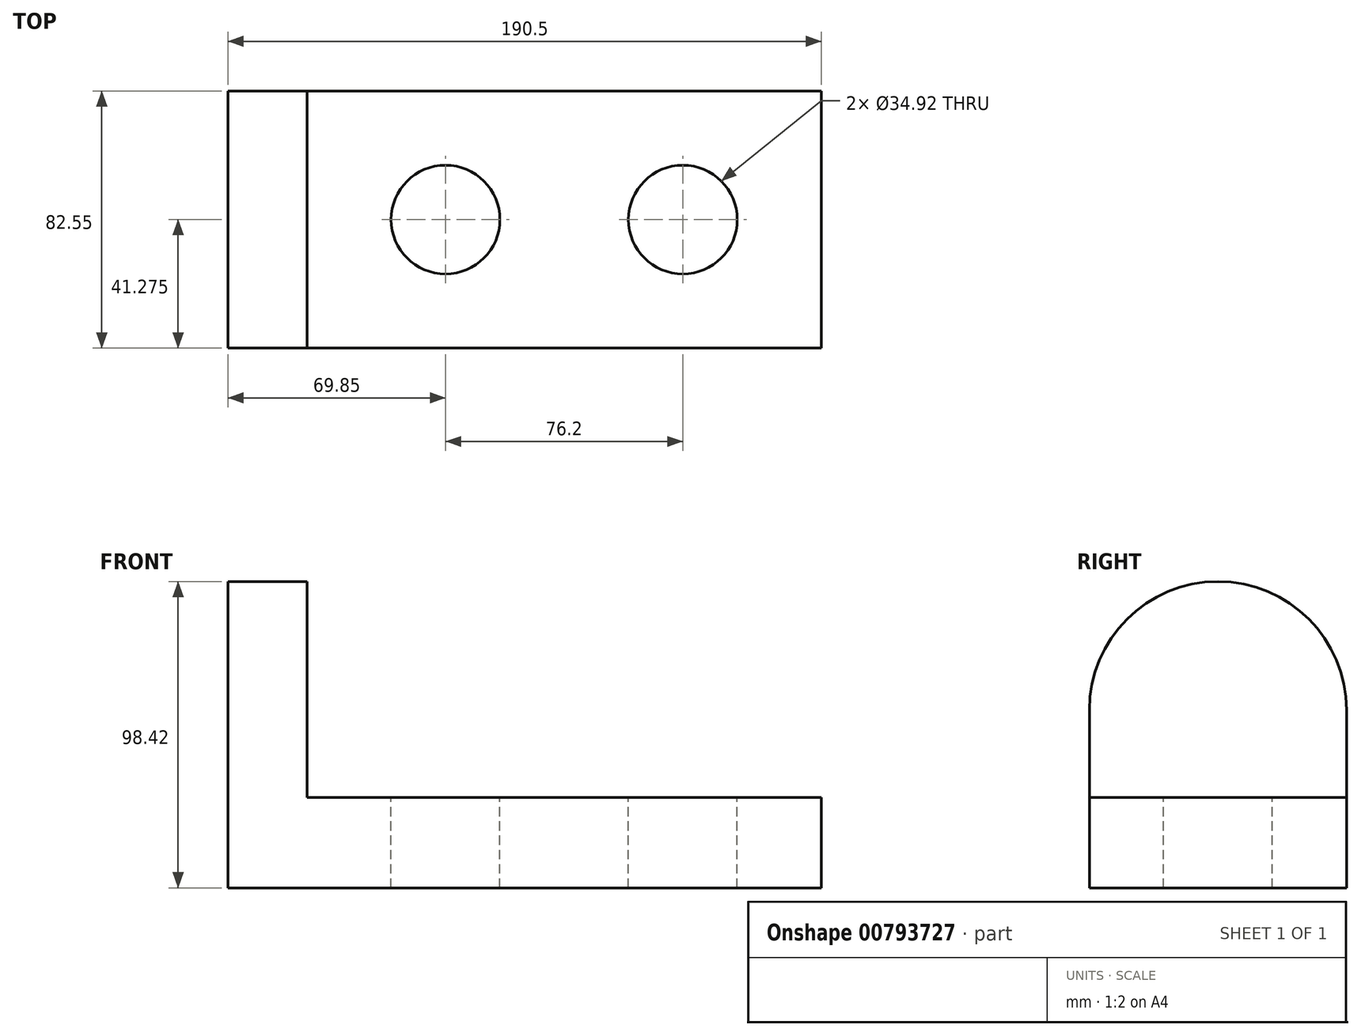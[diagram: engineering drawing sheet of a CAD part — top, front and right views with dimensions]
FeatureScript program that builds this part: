
annotation { "Feature Type Name" : "Feature", "Feature Type Description" : "" }
export const myFeature = defineFeature(function(context is Context, id is Id, definition is map)
    precondition{}
    {
        {
            var Q0;
            Q0=qCreatedBy(makeId("Front.planeOp"),FACE);
            var sketch = newSketch(context, id + "F0", { "sketchPlane" : qUnion([Q0])});
            skLineSegment(sketch, "E0", {"start": v(0, 0) * mm, "end": v(0, 101.6) * mm});
            skLineSegment(sketch, "E1", {"start": v(0, 101.6) * mm, "end": v(25.4, 101.6) * mm});
            skLineSegment(sketch, "E2", {"start": v(0, 0) * mm, "end": v(190.5, 0) * mm});
            skLineSegment(sketch, "E3", {"start": v(190.5, 0) * mm, "end": v(190.5, 29) * mm});
            skLineSegment(sketch, "E4", {"start": v(190.5, 29) * mm, "end": v(25.4, 29) * mm});
            skLineSegment(sketch, "E5", {"start": v(25.4, 29) * mm, "end": v(25.4, 101.6) * mm});
            skSolve(sketch);
        }
        {
            var Q0;
            Q0=makeQuery(id+"F0.imprint","IMPRINT",FACE,{"disambiguationData":[TD([[makeQuery(id+"F0.imprint","IMPRINT",EDGE,{"derivedFrom":sQuery(id+"F0.wireOp",EDGE,"E0")}),-1.0]])]});
            extrude(context, id + "F1", {"entities" : qUnion([Q0]), "depth" : 82.55 * mm, "offsetDistance" : 25.4 * mm});
        }
        {
            var Q0;
            Q0=makeQuery(id+"F1.opExtrude","SWEPT_FACE",FACE,{"disambiguationData":[OSD([sQuery(id+"F0.wireOp",EDGE,"E0")])]});
            var sketch = newSketch(context, id + "F2", { "sketchPlane" : qUnion([Q0])});
            skLineSegment(sketch, "E6", {"start": v(0, 0) * mm, "end": v(0, 57.15) * mm});
            skLineSegment(sketch, "E7", {"start": v(82.55, 0) * mm, "end": v(82.55, 57.15) * mm});
            skLineSegment(sketch, "E8", {"start": v(0, 57.15) * mm, "end": v(41.28, 57.15) * mm});
            skLineSegment(sketch, "E9", {"start": v(41.28, 57.15) * mm, "end": v(82.55, 57.15) * mm});
            skArc(sketch, "E10", {"start": v(82.55, 57.15) * mm, "mid": v(41.28, 98.43) * mm, "end": v(0, 57.15) * mm});
            skSolve(sketch);
        }
        {
            var Q0;
            {var subQ0=sQuery(id+"F2.wireOp",EDGE,"E10");Q0=makeQuery(id+"F2.imprint","IMPRINT",FACE,{"disambiguationData":[TD([[makeQuery(id+"F2.imprint","IMPRINT",EDGE,{"derivedFrom":subQ0}),-1.0]])]});}
            extrude(context, id + "F3", {"entities" : qUnion([Q0]), "operationType" : NewBodyOperationType.REMOVE, "endBound" : BoundingType.THROUGH_ALL, "oppositeDirection" : true, "depth" : 25.4 * mm, "offsetDistance" : 25.4 * mm});
        }
        {
            var Q0;
            Q0=makeQuery(id+"F1.opExtrude","SWEPT_FACE",FACE,{"disambiguationData":[OSD([sQuery(id+"F0.wireOp",EDGE,"E4")])]});
            var sketch = newSketch(context, id + "F4", { "sketchPlane" : qUnion([Q0])});
            skLineSegment(sketch, "E11", {"start": v(25.4, 0) * mm, "end": v(69.85, 0) * mm, "construction": true});
            skLineSegment(sketch, "E12", {"start": v(69.85, 0) * mm, "end": v(146.05, 0) * mm, "construction": true});
            skLineSegment(sketch, "E13", {"start": v(146.05, 0) * mm, "end": v(190.5, 0) * mm, "construction": true});
            skLineSegment(sketch, "E14", {"start": v(69.85, 0) * mm, "end": v(69.85, -41.28) * mm, "construction": true});
            skLineSegment(sketch, "E15", {"start": v(69.85, -41.28) * mm, "end": v(69.85, -82.55) * mm, "construction": true});
            skLineSegment(sketch, "E16", {"start": v(146.05, 0) * mm, "end": v(146.05, -41.28) * mm, "construction": true});
            skLineSegment(sketch, "E17", {"start": v(146.05, -41.28) * mm, "end": v(146.05, -82.55) * mm, "construction": true});
            skCircle(sketch, "E18", {"center": v(69.85, -41.28) * mm, "radius": 17.46 * mm});
            skCircle(sketch, "E19", {"center": v(146.05, -41.28) * mm, "radius": 17.46 * mm});
            skSolve(sketch);
        }
        {
            var Q0;
            Q0=makeQuery(id+"F4.imprint","IMPRINT",FACE,{"disambiguationData":[TD([[makeQuery(id+"F4.imprint","IMPRINT",EDGE,{"derivedFrom":sQuery(id+"F4.wireOp",EDGE,"E18")}),1.0]])]});
            var Q1;
            Q1=makeQuery(id+"F4.imprint","IMPRINT",FACE,{"disambiguationData":[TD([[makeQuery(id+"F4.imprint","IMPRINT",EDGE,{"derivedFrom":sQuery(id+"F4.wireOp",EDGE,"E19")}),1.0]])]});
            extrude(context, id + "F5", {"entities" : qUnion([Q0, Q1]), "operationType" : NewBodyOperationType.REMOVE, "endBound" : BoundingType.THROUGH_ALL, "oppositeDirection" : true, "depth" : 25.4 * mm, "offsetDistance" : 25.4 * mm});
        }
    });
